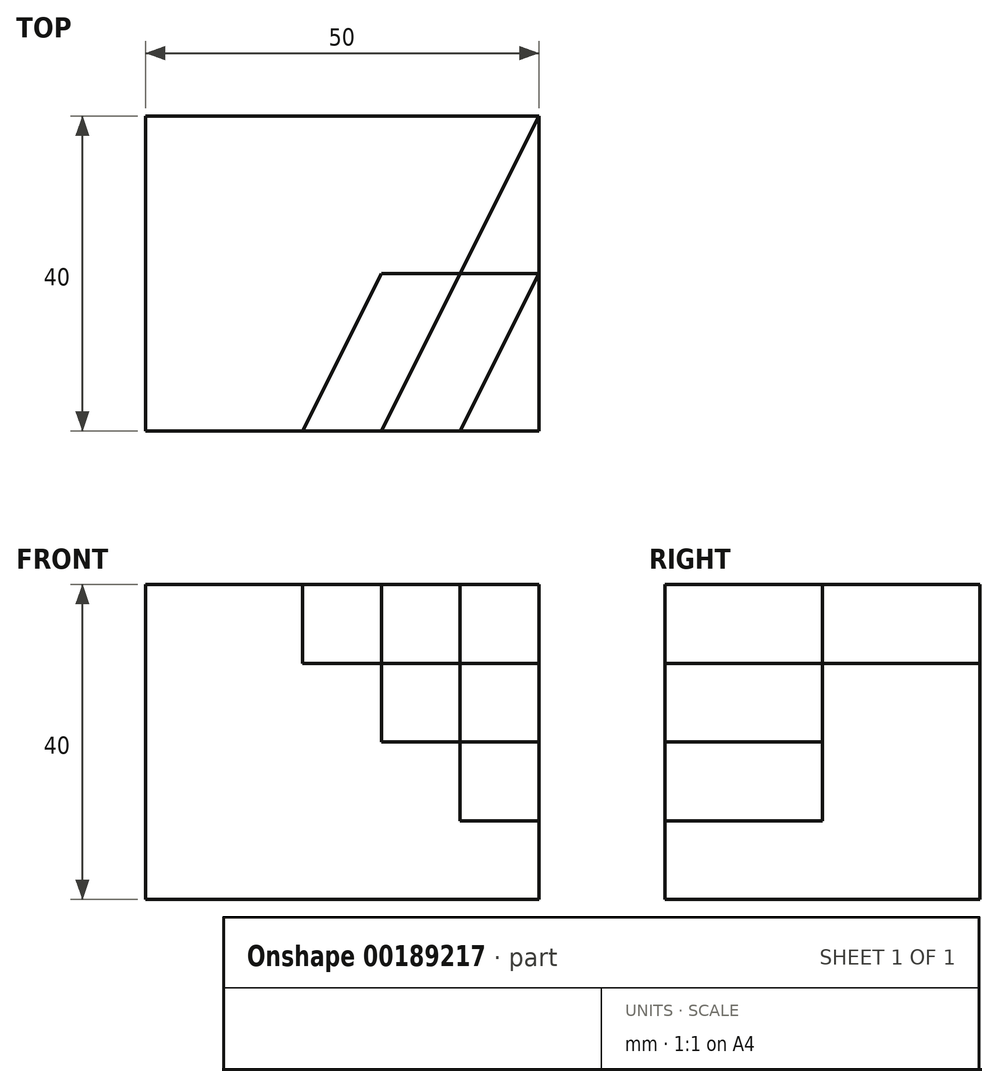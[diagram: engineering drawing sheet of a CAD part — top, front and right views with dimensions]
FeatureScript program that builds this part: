
annotation { "Feature Type Name" : "Feature", "Feature Type Description" : "" }
export const myFeature = defineFeature(function(context is Context, id is Id, definition is map)
    precondition{}
    {
        {
            var Q0;
            Q0=qCreatedBy(makeId("Top.planeOp"),FACE);
            var sketch = newSketch(context, id + "F0", { "sketchPlane" : qUnion([Q0])});
            skLineSegment(sketch, "E0.bottom", {"start": v(0, 0) * mm, "end": v(50, 0) * mm});
            skLineSegment(sketch, "E0.top", {"start": v(0, 40) * mm, "end": v(50, 40) * mm});
            skLineSegment(sketch, "E0.left", {"start": v(0, 0) * mm, "end": v(0, 40) * mm});
            skLineSegment(sketch, "E0.right", {"start": v(50, 0) * mm, "end": v(50, 40) * mm});
            skSolve(sketch);
        }
        {
            var Q0;
            Q0=makeQuery(id+"F0.imprint","IMPRINT",FACE,{"disambiguationData":[TD([[makeQuery(id+"F0.imprint","IMPRINT",EDGE,{"derivedFrom":sQuery(id+"F0.wireOp",EDGE,"E0.bottom")}),1.0]])]});
            extrude(context, id + "F1", {"entities" : qUnion([Q0]), "depth" : 40 * mm});
        }
        {
            var Q0;
            Q0=makeQuery(id+"F1.opExtrude","CAP_FACE",FACE,{"disambiguationData":[OSD([sQuery(id+"F0.wireOp",EDGE,"E0.bottom"),sQuery(id+"F0.wireOp",EDGE,"E0.top"),sQuery(id+"F0.wireOp",EDGE,"E0.left"),sQuery(id+"F0.wireOp",EDGE,"E0.right")])],"isStart":false});
            var sketch = newSketch(context, id + "F2", { "sketchPlane" : qUnion([Q0])});
            skLineSegment(sketch, "E1.0", {"start": v(20, 0) * mm, "end": v(50, 0) * mm});
            skLineSegment(sketch, "E2.0", {"start": v(50, 0) * mm, "end": v(50, 40) * mm});
            skLineSegment(sketch, "E3", {"start": v(20, 0) * mm, "end": v(30, 20) * mm});
            skLineSegment(sketch, "E4", {"start": v(30, 20) * mm, "end": v(40, 20) * mm});
            skLineSegment(sketch, "E5", {"start": v(40, 20) * mm, "end": v(50, 40) * mm});
            skPoint(sketch, "E6.orphan", {"position": v(0, 0) * mm});
            skSolve(sketch);
        }
        {
            var Q0;
            Q0=makeQuery(id+"F2.imprint","IMPRINT",FACE,{"disambiguationData":[TD([[makeQuery(id+"F2.imprint","IMPRINT",EDGE,{"derivedFrom":sQuery(id+"F2.wireOp",EDGE,"E1.0")}),1.0]])]});
            extrude(context, id + "F3", {"entities" : qUnion([Q0]), "operationType" : NewBodyOperationType.REMOVE, "oppositeDirection" : true, "depth" : 10 * mm});
        }
        {
            var Q0;
            Q0=makeQuery(id+"F3.boolean.opBoolean","COPY",FACE,{"derivedFrom":makeQuery(id+"F3.opExtrude","CAP_FACE",FACE,{"disambiguationData":[OSD([sQuery(id+"F2.wireOp",EDGE,"E1.0"),sQuery(id+"F2.wireOp",EDGE,"E2.0"),sQuery(id+"F2.wireOp",EDGE,"E3"),sQuery(id+"F2.wireOp",EDGE,"E4"),sQuery(id+"F2.wireOp",EDGE,"E5")])],"isStart":false})});
            var sketch = newSketch(context, id + "F4", { "sketchPlane" : qUnion([Q0])});
            skLineSegment(sketch, "E7.0", {"start": v(30, 0) * mm, "end": v(50, 0) * mm});
            skLineSegment(sketch, "E8.0", {"start": v(50, 0) * mm, "end": v(50, 20) * mm});
            skLineSegment(sketch, "E9", {"start": v(50, 20) * mm, "end": v(40, 20) * mm});
            skPoint(sketch, "E9.startSnap0", {"position": v(50, 20) * mm});
            skLineSegment(sketch, "E10", {"start": v(40, 20) * mm, "end": v(30, 0) * mm});
            skPoint(sketch, "E11.orphan", {"position": v(20, 0) * mm});
            skPoint(sketch, "E12.orphan", {"position": v(50, 40) * mm});
            skPoint(sketch, "E13.orphan", {"position": v(53.11, 20) * mm});
            skSolve(sketch);
        }
        {
            var Q0;
            Q0=makeQuery(id+"F4.imprint","IMPRINT",FACE,{"disambiguationData":[TD([[makeQuery(id+"F4.imprint","IMPRINT",EDGE,{"derivedFrom":sQuery(id+"F4.wireOp",EDGE,"E7.0")}),1.0]])]});
            extrude(context, id + "F5", {"entities" : qUnion([Q0]), "operationType" : NewBodyOperationType.REMOVE, "oppositeDirection" : true, "depth" : 10 * mm});
        }
        {
            var Q0;
            Q0=makeQuery(id+"F5.boolean.opBoolean","COPY",FACE,{"derivedFrom":makeQuery(id+"F5.opExtrude","CAP_FACE",FACE,{"disambiguationData":[OSD([sQuery(id+"F4.wireOp",EDGE,"E7.0"),sQuery(id+"F4.wireOp",EDGE,"E8.0"),sQuery(id+"F4.wireOp",EDGE,"E9"),sQuery(id+"F4.wireOp",EDGE,"E10")])],"isStart":false})});
            var sketch = newSketch(context, id + "F6", { "sketchPlane" : qUnion([Q0])});
            skLineSegment(sketch, "E14.0", {"start": v(40, 0) * mm, "end": v(50, 0) * mm});
            skLineSegment(sketch, "E15.0", {"start": v(50, 0) * mm, "end": v(50, 20) * mm});
            skLineSegment(sketch, "E16", {"start": v(50, 20) * mm, "end": v(40, 0) * mm});
            skPoint(sketch, "E17.orphan", {"position": v(30, 0) * mm});
            skSolve(sketch);
        }
        {
            var Q0;
            Q0=makeQuery(id+"F6.imprint","IMPRINT",FACE,{"disambiguationData":[TD([[makeQuery(id+"F6.imprint","IMPRINT",EDGE,{"derivedFrom":sQuery(id+"F6.wireOp",EDGE,"E14.0")}),1.0]])]});
            extrude(context, id + "F7", {"entities" : qUnion([Q0]), "operationType" : NewBodyOperationType.REMOVE, "oppositeDirection" : true, "depth" : 10 * mm});
        }
    });
